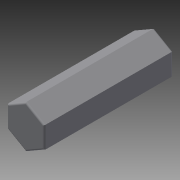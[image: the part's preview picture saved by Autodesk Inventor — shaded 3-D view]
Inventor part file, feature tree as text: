
AUTODESK INVENTOR PART (.ipt)
format: ipt  version: 2015 (Build 190159000, 159)  size: 89,088 bytes
history: native  units: in
note: dims shown in document units (in); Inventor stores cm internally (conversion verified against a paired STEP export)
features: extrude x1, fillet x1, sketch x1
ambient origin geometry x8: Origin, YZ Plane, XZ Plane, XY Plane, X Axis, Y Axis, Z Axis, Center Point
bodies: Solid1 (feature_tree)
feature tree (3):
  extrude  "Extrusion1"  Depth=0.125in
  fillet  "Fillet1"  Radius=0.1083in
  sketch  "Sketch1"  dims[d0=0.25in d1=0.125in d2=0.1083in d3=0.75in d4=0.0in d5=0.01in]
